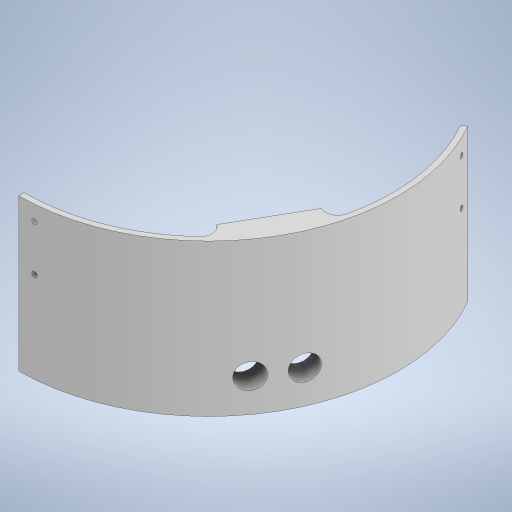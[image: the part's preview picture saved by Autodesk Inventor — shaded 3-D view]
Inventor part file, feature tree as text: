
AUTODESK INVENTOR PART (.ipt)
format: ipt  version: 2023 (Build 270158000, 158)  size: 379,904 bytes
history: native  units: mm
features: sketch x19, extrude x13, hole x6, other x1, fillet x1
ambient origin geometry x8: Origin, YZ Plane, XZ Plane, XY Plane, X Axis, Y Axis, Z Axis, Center Point
bodies: Body1 (feature_tree)
feature tree (40):
  other  "ソリッド1"
  extrude  "押し出し1"  Depth=250.0mm
  extrude  "押し出し2"  Depth=375.0mm TaperAngle=0.0deg
  hole  "穴1"  [1 undecoded]
  hole  "穴2"  [1 undecoded]
  extrude  "押し出し3"  Depth=30.0mm TaperAngle=360.0deg
  extrude  "押し出し4"  Depth=10.0mm
  hole  "穴4"  [1 undecoded]
  hole  "穴5"  [1 undecoded]
  extrude  "押し出し6"  Depth=330.0mm TaperAngle=0.0deg
  extrude  "押し出し7"  Depth=118.0mm
  extrude  "押し出し8"  Depth=30.0mm TaperAngle=360.0deg
  extrude  "押し出し9"  Depth=330.0mm TaperAngle=0.0deg
  extrude  "押し出し11"  Depth=30.0mm
  extrude  "押し出し12"  Depth=30.0mm
  extrude  "押し出し13"  Depth=243.0mm
  extrude  "押し出し14"  Depth=330.0mm TaperAngle=0.0deg
  fillet  "フィレット1"  Radius=125.0mm
  extrude  "押し出し15"  TaperAngle=120.0deg  [1 undecoded]
  hole  "穴6"  [1 undecoded]
  hole  "穴7"  [1 undecoded]
  sketch  "スケッチ1"
  sketch  "スケッチ2"
  sketch  "スケッチ3"
  sketch  "スケッチ4"
  sketch  "スケッチ5"
  sketch  "スケッチ6"
  sketch  "スケッチ8"
  sketch  "スケッチ11"
  sketch  "スケッチ12"
  sketch  "スケッチ13"
  sketch  "スケッチ14"
  sketch  "スケッチ15"
  sketch  "スケッチ17"
  sketch  "スケッチ18"
  sketch  "スケッチ19"
  sketch  "スケッチ20"
  sketch  "スケッチ21"
  sketch  "スケッチ22"
  sketch  "スケッチ23"
note: 7 required parameter values undecoded (feature->parameter linkage not recoverable at this tier; creation-order binding heuristic only, values carry confidence <= 0.55)
